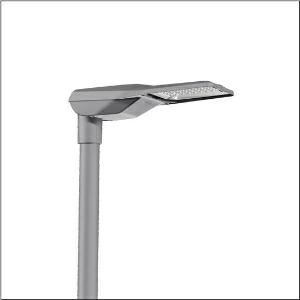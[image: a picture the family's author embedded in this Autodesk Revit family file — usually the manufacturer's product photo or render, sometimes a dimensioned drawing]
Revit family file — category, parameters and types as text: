
# Revit family: streetlight_sl_21_iq_mini___stw1_0a_5xe2e31d08hb_6dd6
name_source: partatom
category: Lighting Fixtures
units: mm (PartAtom-declared; Revit-internal decimal feet)

## family parameters
Cut with Voids When Loaded = No
Host = Face
Light Source = No
Part Type = Normal
Room Calculation Point = No
Round Connector Dimension = Use Diameter
Shared = No

## types (1)
- --- (1 x LED, 9450 lm, 70.9 W, 3000K)
    Apparent Load = 71 VA
    CIE Flux Codes = 38 75 98 100 100
    Color Rendering = 70
    Color Temperature = 3000K
    Default Elevation = 1800 mm
    Description = Streetlight SL 21 iQ mini, mast luminaire, primary light control with lens, of PMMA, primary optical cover: cover, of toughened safety glass, transparent, light distribution: STW1.0a, light emission: direct distribution, primary light characteristic: asymmetric, installation type: post-top, side-entry, LED, High Power LED, rated luminous flux: 9.450lm, luminous efficacy: 133lm/W, light colour: 730, colour temperature: 3000K, control: Auto-Match, Temp-Guard, Lumen-Switch, Night-Set, Smart-Wire, Light-Fading, Desk-Remote (wireless, voltage-free reading and setting of iQ features in the workshop via application-optimized NFC function/RFID function), optimised constant luminous flux control (CLO 2.0), presetting dimming linear, mains connection: 220..240V, AC, 50/60Hz, start of lifetime: 71W, end of service life: 75W, reduction: 31W, luminaire housing, of diecast aluminium, powder-coated, Siteco® metallic grey (DB 702S), corrosivity category C5 mid according to DIN EN ISO 12944, please order mast flange separately, inclination adjustable: 0°, 5°, 10°, 15°, sealing non-destructively replaceable, multi-level sealing system, length: 628mm, width: 235mm, height: 110mm, mast flange for spigot size: 42mm (side-entry): 5XC10008XM4, 60/48mm (side-entry/post-top): 5XC10108XM2, 76/60mm (side-entry/post-top): 5XC10108XM1, protection rating (complete): IP66, insulation class (complete): insulation class II (safety insulation), certification: CE, ENEC, ENEC+, VDE, impact resistance: IK09, permissible operating ambient temperature for outdoor applications: -40..+50°C, standard-compliant lighting for roads and squares, packaging unit: 1 piece

Light Distribution: STW1.0a
    Height = 110 mm
    Lamp = 1 x LED
    Lamp Light Flux = 9450 lm
    Lamp Power = 70.9 W
    Lamp count = 1
    Length = 625 mm
    Luminous efficacy = 133 lm/W
    Manufacturer = Siteco
    ModVariant = No
    Model = 5XE2E31D08HB
    Number of Poles = 1
    OnlyDefault = Yes
    Power Factor = 1
    Product Name = Streetlight SL 21 iQ mini | STW1.0a
    Product group = mast luminaire | pylon top
    ProductGroupID = 6100
    Protection Class = Protection class II
    Protection Degree = IP 66
    RLX_Detail_Level = 1
    RLX_Emergency_Light_Flux = 0 lm
    RLX_Emergency_Type = 0
    RLX_Emergency_Type_DB = No
    RlxData = <blob elided: 93577 chars, md5=b3e7fd53>
    Socket = socket
    Standby Power = 0 W
    System Light Flux = 9450 lm
    System Power = 71 W
    Type Comments = factory setting: luminous flux: 100 % | dim-lin: 254 | 711 mA
    Type Image = l_1003519.jpg
    URL = http://relux.com
    VarID = @adj_108043
    Voltage = 0 V
    Weight = 0.00 kg
    Width = 234 mm

## geometry (parser evidence)
native form markers: Blend x4, Sweep x10
no freeform markers — native parametric forms only
